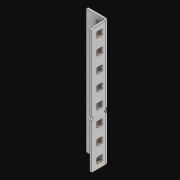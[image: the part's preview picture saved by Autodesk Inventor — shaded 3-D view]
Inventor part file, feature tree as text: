
AUTODESK INVENTOR PART (.ipt)
format: ipt  version: 2021 (Build 250183000, 183)  size: 1,089,536 bytes
history: native  units: in
note: dims shown in document units (in); Inventor stores cm internally (conversion verified against a paired STEP export)
features: extrude x18, other x16, sketch x4, pattern_linear x2, sheet_metal_op x1
ambient origin geometry x8: Origin, YZ Plane, XZ Plane, XY Plane, X Axis, Y Axis, Z Axis, Center Point
bodies: Solid1 (feature_tree)
feature tree (41):
  pattern_linear  "Rectangular Pattern1"  Spacing1=0.5in  [1 undecoded]
  pattern_linear  "Rectangular Pattern3"  Count1=8  [1 undecoded]
  extrude  "Extrusion1"  Depth=0.5in
  extrude  "Extrusion2"  Depth=0.5in
  sketch  "Sketch1"  dims[d0=0.182in]
  other  "Srf1"
  sketch  "Sketch3"  dims[d1=0.063in d2=0.0in]
  other  "Srf3"
  other  "Srf4"
  other  "Srf5"
  other  "Srf6"
  other  "Srf7"
  other  "Srf8"
  other  "Srf9"
  other  "Srf10"
  other  "Srf142"
  other  "Srf143"
  other  "Srf144"
  other  "Srf145"
  other  "Srf146"
  other  "Srf147"
  other  "Srf148"
  sketch  "Sketch4"  dims[d6=0.182in]
  sketch  "Sketch5"  dims[d7=0.063in d8=0.0in d11=0.5in d12=0.3937in d14=0.5in d18=3.1496in d20=0.5in d21=13.5in d22=0.0in d23=0.841in d24=0.0in]
  sheet_metal_op  "Fold1"
  extrude  "ExtrusionSrf1"  TaperAngle=0.0deg  [1 undecoded]
  extrude  "ExtrusionSrf3"  Depth=0.5in TaperAngle=0.0deg
  extrude  "ExtrusionSrf4"  [1 undecoded]
  extrude  "ExtrusionSrf5"  [1 undecoded]
  extrude  "ExtrusionSrf6"  [1 undecoded]
  extrude  "ExtrusionSrf7"  [1 undecoded]
  extrude  "ExtrusionSrf8"  [1 undecoded]
  extrude  "ExtrusionSrf9"  [1 undecoded]
  extrude  "ExtrusionSrf10"  [1 undecoded]
  extrude  "ExtrusionSrf142"  [1 undecoded]
  extrude  "ExtrusionSrf143"  [1 undecoded]
  extrude  "ExtrusionSrf144"  [1 undecoded]
  extrude  "ExtrusionSrf145"  [1 undecoded]
  extrude  "ExtrusionSrf146"  [1 undecoded]
  extrude  "ExtrusionSrf147"  [1 undecoded]
  extrude  "ExtrusionSrf148"  [1 undecoded]
note: 17 required parameter values undecoded (feature->parameter linkage not recoverable at this tier; creation-order binding heuristic only, values carry confidence <= 0.55)
